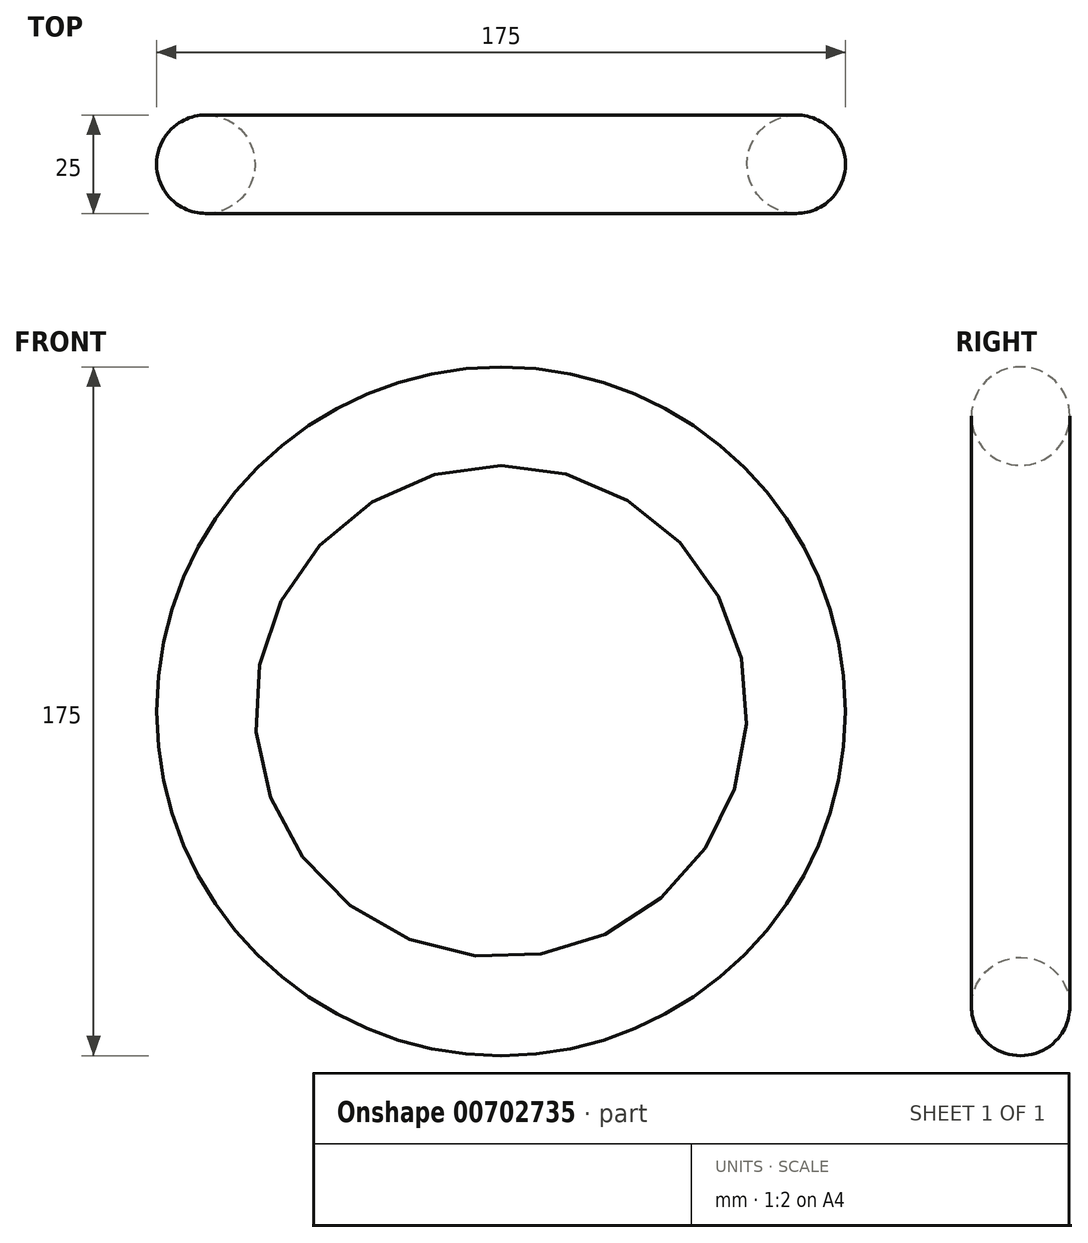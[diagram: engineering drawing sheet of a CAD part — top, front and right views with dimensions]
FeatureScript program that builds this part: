
annotation { "Feature Type Name" : "Feature", "Feature Type Description" : "" }
export const myFeature = defineFeature(function(context is Context, id is Id, definition is map)
    precondition{}
    {
        {
            var Q0;
            Q0=qCreatedBy(makeId("Top.planeOp"),FACE);
            var sketch = newSketch(context, id + "F0", { "sketchPlane" : qUnion([Q0])});
            skLineSegment(sketch, "E0", {"start": v(0, 0) * mm, "end": v(-75, 0) * mm});
            skCircle(sketch, "E1", {"center": v(-75, 0) * mm, "radius": 12.5 * mm});
            skSolve(sketch);
        }
        {
            var Q0;
            Q0=qCreatedBy(makeId("Front.planeOp"),FACE);
            var sketch = newSketch(context, id + "F1", { "sketchPlane" : qUnion([Q0])});
            skCircle(sketch, "E2", {"center": v(0, 0) * mm, "radius": 0.76 * mm});
            skSolve(sketch);
        }
        {
            var Q0;
            Q0=makeQuery(id+"F0.imprint","IMPRINT",FACE,{"disambiguationData":[TD([[makeQuery(id+"F0.imprint","IMPRINT",EDGE,{"derivedFrom":sQuery(id+"F0.wireOp",EDGE,"E1")}),1.0]])]});
            var Q1;
            Q1=sQuery(id+"F1.wireOp",EDGE,"E2");
            revolve(context, id + "F2", {"surfaceOperationType" : NewSurfaceOperationType.NEW, "entities" : qUnion([Q0]), "axis" : qUnion([Q1]), "revolveType" : RevolveType.FULL});
        }
    });
